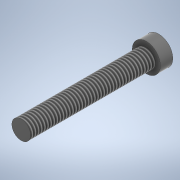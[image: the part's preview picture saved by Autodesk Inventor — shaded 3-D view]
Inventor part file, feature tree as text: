
AUTODESK INVENTOR PART (.ipt)
format: ipt  version: 2020 (Build 240168000, 168)  size: 109,056 bytes
history: native  units: in
note: dims shown in document units (in); Inventor stores cm internally (conversion verified against a paired STEP export)
features: sketch x2, extrude x2, thread x1
ambient origin geometry x8: Origin, YZ Plane, XZ Plane, XY Plane, X Axis, Y Axis, Z Axis, Center Point
bodies: Solid1 (feature_tree)
feature tree (5):
  sketch  "Sketch1"  dims[d0=0.1181in d1=0.1772in]
  extrude  "Extrusion1"  Depth=0.1772in
  extrude  "Extrusion2"  Depth=0.0787in TaperAngle=0.0deg
  thread  "Thread1"  [1 undecoded]
  sketch  "Sketch2"  dims[d2=0.1181in d3=0.1772in d4=0.7874in d5=0.0in d6=0.0787in d7=0.0in d8=0.3937in d9=0.0in]
note: 1 required parameter value undecoded (feature->parameter linkage not recoverable at this tier; creation-order binding heuristic only, values carry confidence <= 0.55)
